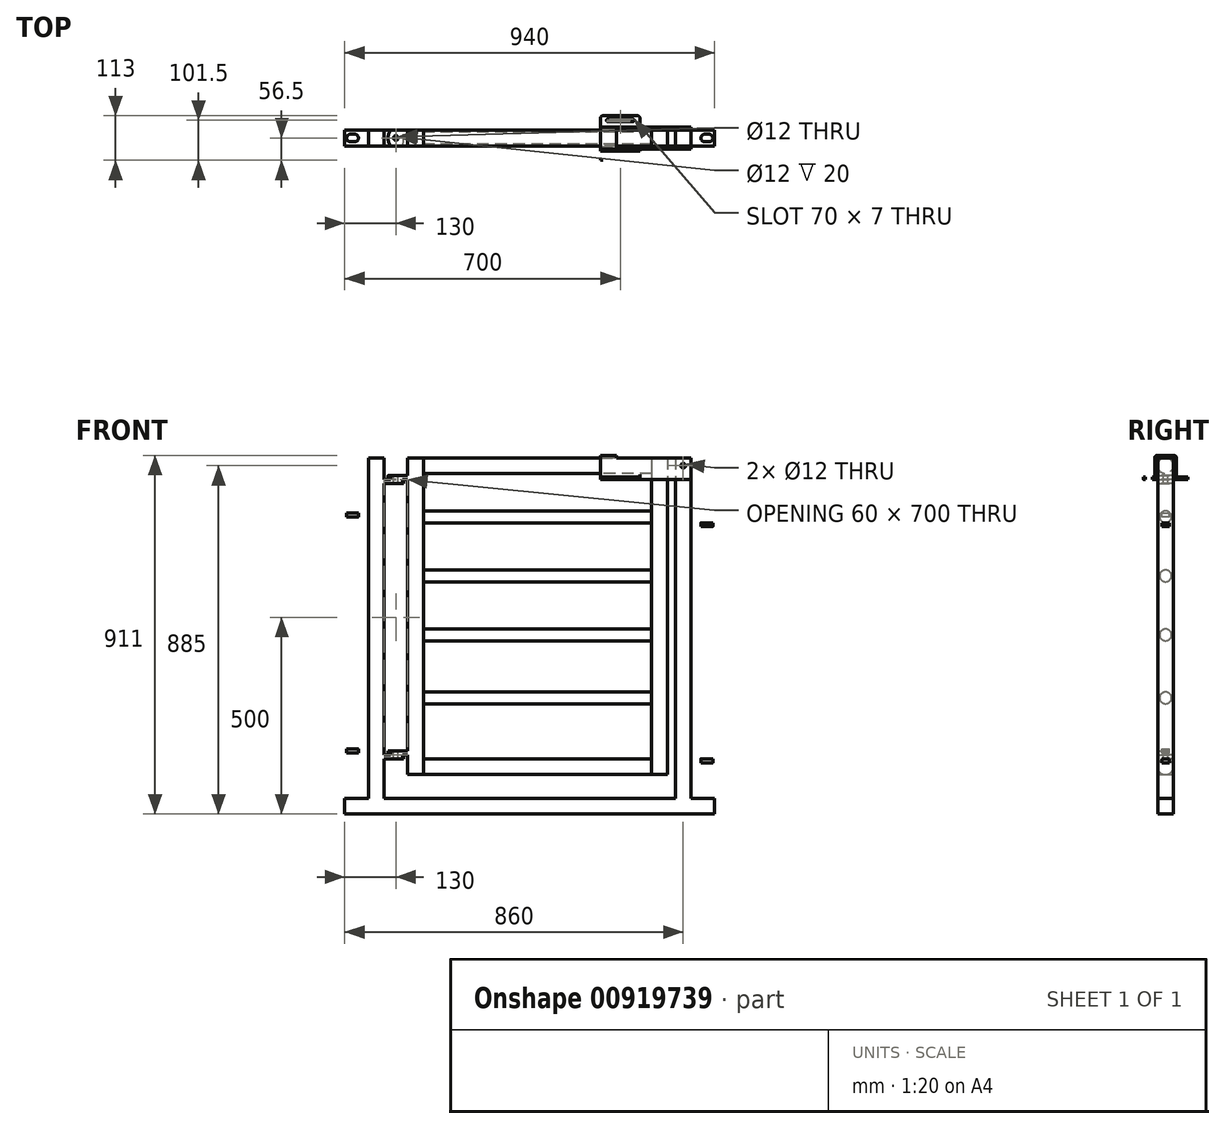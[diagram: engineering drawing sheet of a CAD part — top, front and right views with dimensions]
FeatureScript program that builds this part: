
annotation { "Feature Type Name" : "Feature", "Feature Type Description" : "" }
export const myFeature = defineFeature(function(context is Context, id is Id, definition is map)
    precondition{}
    {
        {
            var Q0;
            Q0=qCreatedBy(makeId("Right.planeOp"),FACE);
            var sketch = newSketch(context, id + "F0", { "sketchPlane" : qUnion([Q0])});
            skLineSegment(sketch, "E0.bottom", {"start": v(-20, 402.5) * mm, "end": v(20, 402.5) * mm});
            skLineSegment(sketch, "E0.top", {"start": v(-20, -402.5) * mm, "end": v(20, -402.5) * mm});
            skLineSegment(sketch, "E0.left", {"start": v(-20, 402.5) * mm, "end": v(-20, -402.5) * mm});
            skLineSegment(sketch, "E0.right", {"start": v(20, 402.5) * mm, "end": v(20, -402.5) * mm});
            skPoint(sketch, "E0.middle", {"position": v(0, 0) * mm});
            skLineSegment(sketch, "E1", {"start": v(0, 402.5) * mm, "end": v(0, -402.5) * mm, "construction": true});
            skPoint(sketch, "E2", {"position": v(0, 382.5) * mm});
            skCircle(sketch, "E3", {"center": v(0, 382.5) * mm, "radius": 20 * mm});
            skPoint(sketch, "E4", {"position": v(0, 252.5) * mm});
            skPoint(sketch, "E5", {"position": v(0, 362.5) * mm});
            skCircle(sketch, "E6", {"center": v(0, 252.5) * mm, "radius": 15 * mm});
            skPoint(sketch, "E7", {"position": v(0, 102.5) * mm});
            skCircle(sketch, "E8", {"center": v(0, 102.5) * mm, "radius": 15 * mm});
            skPoint(sketch, "E9", {"position": v(0, -47.5) * mm});
            skCircle(sketch, "E10", {"center": v(0, -47.5) * mm, "radius": 15 * mm});
            skPoint(sketch, "E11", {"position": v(0, -207.5) * mm});
            skCircle(sketch, "E12", {"center": v(0, -207.5) * mm, "radius": 15 * mm});
            skPoint(sketch, "E13", {"position": v(0, -382.5) * mm});
            skCircle(sketch, "E14", {"center": v(0, -382.5) * mm, "radius": 20 * mm});
            skSolve(sketch);
        }
        {
            var Q0;
            {var subQ0=sQuery(id+"F0.wireOp",EDGE,"E0.left");var subQ1=sQuery(id+"F0.wireOp",EDGE,"E0.bottom");var subQ2=makeQuery(id+"F0.imprint","INTERSECT",VERTEX,{"derivedFrom":[subQ1,subQ0]});Q0=makeQuery(id+"F0.imprint","IMPRINT",FACE,{"disambiguationData":[TD([[makeQuery(id+"F0.imprint","IMPRINT",EDGE,{"disambiguationData":[TD([[subQ2,-1.0]])],"derivedFrom":subQ1}),-1.0]])]});}
            var Q1;
            {var subQ0=sQuery(id+"F0.wireOp",EDGE,"E0.right");var subQ1=sQuery(id+"F0.wireOp",EDGE,"E0.bottom");var subQ2=makeQuery(id+"F0.imprint","INTERSECT",VERTEX,{"derivedFrom":[subQ1,subQ0]});Q1=makeQuery(id+"F0.imprint","IMPRINT",FACE,{"disambiguationData":[TD([[makeQuery(id+"F0.imprint","IMPRINT",EDGE,{"disambiguationData":[TD([[subQ2,1.0]])],"derivedFrom":subQ1}),-1.0]])]});}
            var Q2;
            Q2=makeQuery(id+"F0.imprint","IMPRINT",FACE,{"disambiguationData":[TD([[makeQuery(id+"F0.imprint","IMPRINT",EDGE,{"derivedFrom":sQuery(id+"F0.wireOp",EDGE,"E6")}),-1.0]])]});
            var Q3;
            {var subQ0=sQuery(id+"F0.wireOp",EDGE,"E0.right");var subQ1=sQuery(id+"F0.wireOp",EDGE,"E0.top");var subQ2=makeQuery(id+"F0.imprint","INTERSECT",VERTEX,{"derivedFrom":[subQ1,subQ0]});Q3=makeQuery(id+"F0.imprint","IMPRINT",FACE,{"disambiguationData":[TD([[makeQuery(id+"F0.imprint","IMPRINT",EDGE,{"disambiguationData":[TD([[subQ2,1.0]])],"derivedFrom":subQ1}),1.0]])]});}
            var Q4;
            {var subQ0=sQuery(id+"F0.wireOp",EDGE,"E0.left");var subQ1=sQuery(id+"F0.wireOp",EDGE,"E0.top");var subQ2=makeQuery(id+"F0.imprint","INTERSECT",VERTEX,{"derivedFrom":[subQ1,subQ0]});Q4=makeQuery(id+"F0.imprint","IMPRINT",FACE,{"disambiguationData":[TD([[makeQuery(id+"F0.imprint","IMPRINT",EDGE,{"disambiguationData":[TD([[subQ2,-1.0]])],"derivedFrom":subQ1}),1.0]])]});}
            var Q5;
            {var subQ0=sQuery(id+"F0.wireOp",EDGE,"E3");var subQ1=makeQuery(id+"F0.imprint","INTERSECT",VERTEX,{"derivedFrom":[sQuery(id+"F0.wireOp",EDGE,"E0.bottom"),subQ0]});Q5=makeQuery(id+"F0.imprint","IMPRINT",FACE,{"disambiguationData":[TD([[makeQuery(id+"F0.imprint","IMPRINT",EDGE,{"disambiguationData":[TD([[subQ1,1.0]])],"derivedFrom":subQ0}),1.0]])]});}
            var Q6;
            Q6=makeQuery(id+"F0.imprint","IMPRINT",FACE,{"disambiguationData":[TD([[makeQuery(id+"F0.imprint","IMPRINT",EDGE,{"derivedFrom":sQuery(id+"F0.wireOp",EDGE,"E6")}),1.0]])]});
            var Q7;
            Q7=makeQuery(id+"F0.imprint","IMPRINT",FACE,{"disambiguationData":[TD([[makeQuery(id+"F0.imprint","IMPRINT",EDGE,{"derivedFrom":sQuery(id+"F0.wireOp",EDGE,"E8")}),1.0]])]});
            var Q8;
            Q8=makeQuery(id+"F0.imprint","IMPRINT",FACE,{"disambiguationData":[TD([[makeQuery(id+"F0.imprint","IMPRINT",EDGE,{"derivedFrom":sQuery(id+"F0.wireOp",EDGE,"E10")}),1.0]])]});
            var Q9;
            Q9=makeQuery(id+"F0.imprint","IMPRINT",FACE,{"disambiguationData":[TD([[makeQuery(id+"F0.imprint","IMPRINT",EDGE,{"derivedFrom":sQuery(id+"F0.wireOp",EDGE,"E12")}),1.0]])]});
            var Q10;
            {var subQ0=sQuery(id+"F0.wireOp",EDGE,"E14");var subQ1=makeQuery(id+"F0.imprint","INTERSECT",VERTEX,{"derivedFrom":[sQuery(id+"F0.wireOp",EDGE,"E0.left"),subQ0]});Q10=makeQuery(id+"F0.imprint","IMPRINT",FACE,{"disambiguationData":[TD([[makeQuery(id+"F0.imprint","IMPRINT",EDGE,{"disambiguationData":[TD([[subQ1,1.0]])],"derivedFrom":subQ0}),1.0]])]});}
            extrude(context, id + "F1", {"entities" : qUnion([Q0, Q1, Q2, Q3, Q4, Q5, Q6, Q7, Q8, Q9, Q10]), "depth" : 40 * mm, "offsetDistance" : 25 * mm});
        }
        {
            var Q0;
            Q0=makeQuery(id+"F1.opExtrude","CAP_FACE",FACE,{"disambiguationData":[OSD([sQuery(id+"F0.wireOp",EDGE,"E0.bottom"),sQuery(id+"F0.wireOp",EDGE,"E0.top"),sQuery(id+"F0.wireOp",EDGE,"E0.left"),sQuery(id+"F0.wireOp",EDGE,"E0.right")])],"isStart":false});
            cPlane(context, id + "F2", {"entities" : qUnion([Q0]), "cplaneType" : CPlaneType.OFFSET, "offset" : (580 / 2) * mm, "width" : 150 * mm, "height" : 150 * mm});
        }
        {
            var Q0;
            Q0=makeQuery(id+"F1.opExtrude","SWEPT_BODY",BODY,{"disambiguationData":[OSD([sQuery(id+"F0.wireOp",EDGE,"E0.bottom"),sQuery(id+"F0.wireOp",EDGE,"E0.top"),sQuery(id+"F0.wireOp",EDGE,"E0.left"),sQuery(id+"F0.wireOp",EDGE,"E0.right")])]});
            var Q1;
            Q1=qCreatedBy(id+"F2.planeOp",FACE);
            mirror(context, id + "F3", {"entities" : qUnion([Q0]), "mirrorPlane" : qUnion([Q1])});
        }
        {
            var Q0;
            {var subQ0=sQuery(id+"F0.wireOp",EDGE,"E3");var subQ1=makeQuery(id+"F0.imprint","INTERSECT",VERTEX,{"derivedFrom":[sQuery(id+"F0.wireOp",EDGE,"E0.bottom"),subQ0]});Q0=makeQuery(id+"F0.imprint","IMPRINT",FACE,{"disambiguationData":[TD([[makeQuery(id+"F0.imprint","IMPRINT",EDGE,{"disambiguationData":[TD([[subQ1,1.0]])],"derivedFrom":subQ0}),1.0]])]});}
            var Q1;
            Q1=makeQuery(id+"F0.imprint","IMPRINT",FACE,{"disambiguationData":[TD([[makeQuery(id+"F0.imprint","IMPRINT",EDGE,{"derivedFrom":sQuery(id+"F0.wireOp",EDGE,"E6")}),1.0]])]});
            var Q2;
            Q2=makeQuery(id+"F0.imprint","IMPRINT",FACE,{"disambiguationData":[TD([[makeQuery(id+"F0.imprint","IMPRINT",EDGE,{"derivedFrom":sQuery(id+"F0.wireOp",EDGE,"E8")}),1.0]])]});
            var Q3;
            Q3=makeQuery(id+"F0.imprint","IMPRINT",FACE,{"disambiguationData":[TD([[makeQuery(id+"F0.imprint","IMPRINT",EDGE,{"derivedFrom":sQuery(id+"F0.wireOp",EDGE,"E10")}),1.0]])]});
            var Q4;
            Q4=makeQuery(id+"F0.imprint","IMPRINT",FACE,{"disambiguationData":[TD([[makeQuery(id+"F0.imprint","IMPRINT",EDGE,{"derivedFrom":sQuery(id+"F0.wireOp",EDGE,"E12")}),1.0]])]});
            var Q5;
            {var subQ0=sQuery(id+"F0.wireOp",EDGE,"E14");var subQ1=makeQuery(id+"F0.imprint","INTERSECT",VERTEX,{"derivedFrom":[sQuery(id+"F0.wireOp",EDGE,"E0.left"),subQ0]});Q5=makeQuery(id+"F0.imprint","IMPRINT",FACE,{"disambiguationData":[TD([[makeQuery(id+"F0.imprint","IMPRINT",EDGE,{"disambiguationData":[TD([[subQ1,1.0]])],"derivedFrom":subQ0}),1.0]])]});}
            var Q6;
            Q6=makeQuery(id+"F3.opPattern","COPY",FACE,{"derivedFrom":makeQuery(id+"F1.opExtrude","CAP_FACE",FACE,{"disambiguationData":[OSD([sQuery(id+"F0.wireOp",EDGE,"E0.bottom"),sQuery(id+"F0.wireOp",EDGE,"E0.top"),sQuery(id+"F0.wireOp",EDGE,"E0.left"),sQuery(id+"F0.wireOp",EDGE,"E0.right")])],"isStart":false}),"instanceName":"1"});
            extrude(context, id + "F4", {"entities" : qUnion([Q0, Q1, Q2, Q3, Q4, Q5]), "operationType" : NewBodyOperationType.ADD, "endBound" : BoundingType.UP_TO_SURFACE, "depth" : 25 * mm, "endBoundEntityFace" : qUnion([Q6]), "offsetDistance" : 25 * mm});
        }
        {
            var Q0;
            Q0=makeQuery(id+"F1.opExtrude","CAP_FACE",FACE,{"disambiguationData":[OSD([sQuery(id+"F0.wireOp",EDGE,"E0.bottom"),sQuery(id+"F0.wireOp",EDGE,"E0.top"),sQuery(id+"F0.wireOp",EDGE,"E0.left"),sQuery(id+"F0.wireOp",EDGE,"E0.right")])],"isStart":true});
            var sketch = newSketch(context, id + "F5", { "sketchPlane" : qUnion([Q0])});
            skLineSegment(sketch, "E15.0.0", {"start": v(-20, 402.5) * mm, "end": v(-20, -402.5) * mm});
            skLineSegment(sketch, "E15.0.1", {"start": v(-20, -402.5) * mm, "end": v(20, -402.5) * mm});
            skLineSegment(sketch, "E15.0.2", {"start": v(20, -402.5) * mm, "end": v(20, 402.5) * mm});
            skLineSegment(sketch, "E15.0.3", {"start": v(20, 402.5) * mm, "end": v(-20, 402.5) * mm});
            skLineSegment(sketch, "E16.bottom", {"start": v(20, 357.5) * mm, "end": v(-20, 357.5) * mm});
            skLineSegment(sketch, "E16.top", {"start": v(20, 347.5) * mm, "end": v(-20, 347.5) * mm});
            skLineSegment(sketch, "E16.left", {"start": v(20, 357.5) * mm, "end": v(20, 347.5) * mm});
            skLineSegment(sketch, "E16.right", {"start": v(-20, 357.5) * mm, "end": v(-20, 347.5) * mm});
            skLineSegment(sketch, "E17.bottom", {"start": v(20, -342.5) * mm, "end": v(-20, -342.5) * mm});
            skLineSegment(sketch, "E17.top", {"start": v(20, -352.5) * mm, "end": v(-20, -352.5) * mm});
            skLineSegment(sketch, "E17.left", {"start": v(20, -342.5) * mm, "end": v(20, -352.5) * mm});
            skLineSegment(sketch, "E17.right", {"start": v(-20, -342.5) * mm, "end": v(-20, -352.5) * mm});
            skSolve(sketch);
        }
        {
            var Q0;
            Q0=makeQuery(id+"F5.imprint","IMPRINT",FACE,{"disambiguationData":[TD([[makeQuery(id+"F5.imprint","IMPRINT",EDGE,{"derivedFrom":sQuery(id+"F5.wireOp",EDGE,"E17.bottom")}),1.0]])]});
            var Q1;
            Q1=makeQuery(id+"F5.imprint","IMPRINT",FACE,{"disambiguationData":[TD([[makeQuery(id+"F5.imprint","IMPRINT",EDGE,{"derivedFrom":sQuery(id+"F5.wireOp",EDGE,"E16.bottom")}),1.0]])]});
            extrude(context, id + "F6", {"entities" : qUnion([Q0, Q1]), "operationType" : NewBodyOperationType.ADD, "depth" : 50 * mm, "offsetDistance" : 25 * mm});
        }
        {
            var Q0;
            Q0=makeQuery(id+"F6.opExtrude","SWEPT_FACE",FACE,{"disambiguationData":[OSD([sQuery(id+"F5.wireOp",EDGE,"E16.bottom")])]});
            var sketch = newSketch(context, id + "F7", { "sketchPlane" : qUnion([Q0])});
            skLineSegment(sketch, "E18.0.0", {"start": v(0, -20) * mm, "end": v(0, 20) * mm});
            skLineSegment(sketch, "E18.0.1", {"start": v(0, 20) * mm, "end": v(-50, 20) * mm});
            skLineSegment(sketch, "E18.0.2", {"start": v(-50, 20) * mm, "end": v(-50, -20) * mm});
            skLineSegment(sketch, "E18.0.3", {"start": v(-50, -20) * mm, "end": v(0, -20) * mm});
            skLineSegment(sketch, "E19", {"start": v(-30, 0) * mm, "end": v(0, 0) * mm, "construction": true});
            skPoint(sketch, "E20", {"position": v(-30, 0) * mm});
            skPoint(sketch, "E21", {"position": v(-50, 0) * mm});
            skLineSegment(sketch, "E22", {"start": v(-44.1, 20) * mm, "end": v(-44.1, -20) * mm, "construction": true});
            skArc(sketch, "E23", {"start": v(-44.1, 20) * mm, "mid": v(-50, 0) * mm, "end": v(-44.1, -20) * mm});
            skSolve(sketch);
        }
        {
            var Q0;
            Q0=sQuery(id+"F7.wireOp",VERTEX,"E20");
            var Q1;
            Q1=makeQuery(id+"F1.opExtrude","SWEPT_BODY",BODY,{"disambiguationData":[OSD([sQuery(id+"F0.wireOp",EDGE,"E0.bottom"),sQuery(id+"F0.wireOp",EDGE,"E0.top"),sQuery(id+"F0.wireOp",EDGE,"E0.left"),sQuery(id+"F0.wireOp",EDGE,"E0.right")])]});
            hole(context, id + "F8", {"style" : HoleStyle.SIMPLE, "endStyle" : HoleEndStyle.THROUGH, "standardTappedOrClearance" : lookupTablePath({ "standard" : "ISO", "size" : "12", "type" : "Drilled" }), "standardBlindInLast" : lookupTablePath({ "standard" : "ISO", "size" : "12", "type" : "Drilled" }), "holeDiameter" : 12 * mm, "majorDiameter" : 5 * mm, "isTappedThrough" : true, "tappedDepth" : 12 * mm, "tapClearance" : 3, "startFromSketch" : true, "locations" : qUnion([Q0]), "scope" : qUnion([Q1])});
        }
        {
            var Q0;
            {var subQ0=sQuery(id+"F7.wireOp",EDGE,"E18.0.2");var subQ1=sQuery(id+"F7.wireOp",EDGE,"E18.0.1");var subQ2=makeQuery(id+"F7.imprint","INTERSECT",VERTEX,{"derivedFrom":[subQ1,subQ0]});Q0=makeQuery(id+"F7.imprint","IMPRINT",FACE,{"disambiguationData":[TD([[makeQuery(id+"F7.imprint","IMPRINT",EDGE,{"disambiguationData":[TD([[subQ2,-1.0]])],"derivedFrom":subQ1}),-1.0]])]});}
            var Q1;
            {var subQ0=sQuery(id+"F7.wireOp",EDGE,"E18.0.3");var subQ1=sQuery(id+"F7.wireOp",EDGE,"E18.0.2");var subQ2=makeQuery(id+"F7.imprint","INTERSECT",VERTEX,{"derivedFrom":[subQ1,subQ0]});Q1=makeQuery(id+"F7.imprint","IMPRINT",FACE,{"disambiguationData":[TD([[makeQuery(id+"F7.imprint","IMPRINT",EDGE,{"disambiguationData":[TD([[subQ2,-1.0]])],"derivedFrom":subQ1}),-1.0]])]});}
            extrude(context, id + "F9", {"entities" : qUnion([Q0, Q1]), "operationType" : NewBodyOperationType.REMOVE, "endBound" : BoundingType.THROUGH_ALL, "oppositeDirection" : true, "depth" : 25 * mm, "offsetDistance" : 25 * mm});
        }
        {
            var Q0;
            Q0=qCreatedBy(makeId("Right.planeOp"),FACE);
            cPlane(context, id + "F10", {"entities" : qUnion([Q0]), "cplaneType" : CPlaneType.OFFSET, "offset" : 60 * mm, "oppositeDirection" : true, "width" : 150 * mm, "height" : 150 * mm});
        }
        {
            var Q0;
            Q0=qCreatedBy(id+"F10.planeOp",FACE);
            var sketch = newSketch(context, id + "F11", { "sketchPlane" : qUnion([Q0])});
            skPoint(sketch, "E24.0", {"position": v(20, 402.5) * mm});
            skLineSegment(sketch, "E25.bottom", {"start": v(20, 402.5) * mm, "end": v(-20, 402.5) * mm});
            skLineSegment(sketch, "E25.top", {"start": v(20, -502.5) * mm, "end": v(-20, -502.5) * mm});
            skLineSegment(sketch, "E25.left", {"start": v(20, 402.5) * mm, "end": v(20, -502.5) * mm});
            skLineSegment(sketch, "E25.right", {"start": v(-20, 402.5) * mm, "end": v(-20, -502.5) * mm});
            skSolve(sketch);
        }
        {
            var Q0;
            Q0=makeQuery(id+"F11.imprint","IMPRINT",FACE,{"disambiguationData":[TD([[makeQuery(id+"F11.imprint","IMPRINT",EDGE,{"derivedFrom":sQuery(id+"F11.wireOp",EDGE,"E25.bottom")}),1.0]])]});
            extrude(context, id + "F12", {"entities" : qUnion([Q0]), "oppositeDirection" : true, "depth" : 40 * mm, "offsetDistance" : 25 * mm});
        }
        {
            var Q0;
            Q0=makeQuery(id+"F12.opExtrude","CAP_FACE",FACE,{"disambiguationData":[OSD([sQuery(id+"F11.wireOp",EDGE,"E25.bottom"),sQuery(id+"F11.wireOp",EDGE,"E25.top"),sQuery(id+"F11.wireOp",EDGE,"E25.left"),sQuery(id+"F11.wireOp",EDGE,"E25.right")])],"isStart":false});
            var sketch = newSketch(context, id + "F13", { "sketchPlane" : qUnion([Q0])});
            skLineSegment(sketch, "E26.0.0", {"start": v(-20, -502.5) * mm, "end": v(20, -502.5) * mm});
            skLineSegment(sketch, "E26.0.1", {"start": v(20, -502.5) * mm, "end": v(20, 402.5) * mm});
            skLineSegment(sketch, "E26.0.2", {"start": v(20, 402.5) * mm, "end": v(-20, 402.5) * mm});
            skLineSegment(sketch, "E26.0.3", {"start": v(-20, 402.5) * mm, "end": v(-20, -502.5) * mm});
            skLineSegment(sketch, "E27.top", {"start": v(-20, -462.5) * mm, "end": v(20, -462.5) * mm});
            skLineSegment(sketch, "E27.left", {"start": v(-20, -502.5) * mm, "end": v(-20, -462.5) * mm});
            skLineSegment(sketch, "E27.right", {"start": v(20, -502.5) * mm, "end": v(20, -462.5) * mm});
            skSolve(sketch);
        }
        {
            var Q0;
            Q0=makeQuery(id+"F13.imprint","IMPRINT",FACE,{"disambiguationData":[TD([[makeQuery(id+"F13.imprint","IMPRINT",EDGE,{"derivedFrom":sQuery(id+"F13.wireOp",EDGE,"E26.0.0")}),1.0]])]});
            extrude(context, id + "F14", {"entities" : qUnion([Q0]), "oppositeDirection" : true, "depth" : 880 * mm, "offsetDistance" : 25 * mm, "hasSecondDirection" : true, "secondDirectionOppositeDirection" : false, "secondDirectionDepth" : 60 * mm});
        }
        {
            var Q0;
            Q0=makeQuery(id+"F12.opExtrude","CAP_FACE",FACE,{"disambiguationData":[OSD([sQuery(id+"F11.wireOp",EDGE,"E25.bottom"),sQuery(id+"F11.wireOp",EDGE,"E25.top"),sQuery(id+"F11.wireOp",EDGE,"E25.left"),sQuery(id+"F11.wireOp",EDGE,"E25.right")])],"isStart":true});
            cPlane(context, id + "F15", {"entities" : qUnion([Q0]), "cplaneType" : CPlaneType.OFFSET, "offset" : (740 / 2) * mm, "width" : 150 * mm, "height" : 150 * mm});
        }
        {
            var Q0;
            Q0=makeQuery(id+"F12.opExtrude","SWEPT_BODY",BODY,{"disambiguationData":[OSD([sQuery(id+"F11.wireOp",EDGE,"E25.bottom"),sQuery(id+"F11.wireOp",EDGE,"E25.top"),sQuery(id+"F11.wireOp",EDGE,"E25.left"),sQuery(id+"F11.wireOp",EDGE,"E25.right")])]});
            var Q1;
            Q1=qCreatedBy(id+"F15.planeOp",FACE);
            mirror(context, id + "F16", {"operationType" : NewBodyOperationType.ADD, "entities" : qUnion([Q0]), "mirrorPlane" : qUnion([Q1])});
        }
        {
            var Q0;
            Q0=makeQuery(id+"F16.opPattern","COPY",FACE,{"derivedFrom":makeQuery(id+"F12.opExtrude","CAP_FACE",FACE,{"disambiguationData":[OSD([sQuery(id+"F11.wireOp",EDGE,"E25.bottom"),sQuery(id+"F11.wireOp",EDGE,"E25.top"),sQuery(id+"F11.wireOp",EDGE,"E25.left"),sQuery(id+"F11.wireOp",EDGE,"E25.right")])],"isStart":false}),"instanceName":"1"});
            var sketch = newSketch(context, id + "F17", { "sketchPlane" : qUnion([Q0])});
            skLineSegment(sketch, "E28.0.0", {"start": v(-20, 402.5) * mm, "end": v(-20, -462.5) * mm});
            skLineSegment(sketch, "E28.0.1", {"start": v(-20, -462.5) * mm, "end": v(20, -462.5) * mm});
            skLineSegment(sketch, "E28.0.2", {"start": v(20, -462.5) * mm, "end": v(20, 402.5) * mm});
            skLineSegment(sketch, "E28.0.3", {"start": v(20, 402.5) * mm, "end": v(-20, 402.5) * mm});
            skLineSegment(sketch, "E29.bottom", {"start": v(-20, 237.5) * mm, "end": v(20, 237.5) * mm});
            skLineSegment(sketch, "E29.top", {"start": v(-20, 227.5) * mm, "end": v(20, 227.5) * mm});
            skLineSegment(sketch, "E29.left", {"start": v(-20, 237.5) * mm, "end": v(-20, 227.5) * mm});
            skLineSegment(sketch, "E29.right", {"start": v(20, 237.5) * mm, "end": v(20, 227.5) * mm});
            skPoint(sketch, "E30.0", {"position": v(0, -502.5) * mm});
            skLineSegment(sketch, "E31.bottom", {"start": v(-20, -362.5) * mm, "end": v(20, -362.5) * mm});
            skLineSegment(sketch, "E31.top", {"start": v(-20, -372.5) * mm, "end": v(20, -372.5) * mm});
            skLineSegment(sketch, "E31.left", {"start": v(-20, -362.5) * mm, "end": v(-20, -372.5) * mm});
            skLineSegment(sketch, "E31.right", {"start": v(20, -362.5) * mm, "end": v(20, -372.5) * mm});
            skSolve(sketch);
        }
        {
            var Q0;
            Q0=makeQuery(id+"F17.imprint","IMPRINT",FACE,{"disambiguationData":[TD([[makeQuery(id+"F17.imprint","IMPRINT",EDGE,{"derivedFrom":sQuery(id+"F17.wireOp",EDGE,"E29.bottom")}),-1.0]])]});
            var Q1;
            Q1=makeQuery(id+"F17.imprint","IMPRINT",FACE,{"disambiguationData":[TD([[makeQuery(id+"F17.imprint","IMPRINT",EDGE,{"derivedFrom":sQuery(id+"F17.wireOp",EDGE,"E31.bottom")}),-1.0]])]});
            extrude(context, id + "F18", {"entities" : qUnion([Q0, Q1]), "operationType" : NewBodyOperationType.ADD, "depth" : 65 * mm, "offsetDistance" : 25 * mm});
        }
        {
            var Q0;
            Q0=makeQuery(id+"F12.opExtrude","CAP_FACE",FACE,{"disambiguationData":[OSD([sQuery(id+"F11.wireOp",EDGE,"E25.bottom"),sQuery(id+"F11.wireOp",EDGE,"E25.top"),sQuery(id+"F11.wireOp",EDGE,"E25.left"),sQuery(id+"F11.wireOp",EDGE,"E25.right")])],"isStart":false});
            var sketch = newSketch(context, id + "F19", { "sketchPlane" : qUnion([Q0])});
            skLineSegment(sketch, "E32.0.0", {"start": v(-20, -462.5) * mm, "end": v(20, -462.5) * mm});
            skLineSegment(sketch, "E32.0.1", {"start": v(20, -462.5) * mm, "end": v(20, 402.5) * mm});
            skLineSegment(sketch, "E32.0.2", {"start": v(20, 402.5) * mm, "end": v(-20, 402.5) * mm});
            skLineSegment(sketch, "E32.0.3", {"start": v(-20, 402.5) * mm, "end": v(-20, -462.5) * mm});
            skLineSegment(sketch, "E33.0.0", {"start": v(20, -462.5) * mm, "end": v(-20, -462.5) * mm});
            skLineSegment(sketch, "E33.0.1", {"start": v(-20, -462.5) * mm, "end": v(-20, -502.5) * mm});
            skLineSegment(sketch, "E33.0.2", {"start": v(-20, -502.5) * mm, "end": v(20, -502.5) * mm});
            skLineSegment(sketch, "E33.0.3", {"start": v(20, -502.5) * mm, "end": v(20, -462.5) * mm});
            skLineSegment(sketch, "E34.bottom", {"start": v(20, -347.5) * mm, "end": v(-20, -347.5) * mm});
            skLineSegment(sketch, "E34.top", {"start": v(20, -337.5) * mm, "end": v(-20, -337.5) * mm});
            skLineSegment(sketch, "E34.left", {"start": v(20, -347.5) * mm, "end": v(20, -337.5) * mm});
            skLineSegment(sketch, "E34.right", {"start": v(-20, -347.5) * mm, "end": v(-20, -337.5) * mm});
            skLineSegment(sketch, "E35.bottom", {"start": v(-20, 252.5) * mm, "end": v(20, 252.5) * mm});
            skLineSegment(sketch, "E35.top", {"start": v(-20, 262.5) * mm, "end": v(20, 262.5) * mm});
            skLineSegment(sketch, "E35.left", {"start": v(-20, 252.5) * mm, "end": v(-20, 262.5) * mm});
            skLineSegment(sketch, "E35.right", {"start": v(20, 252.5) * mm, "end": v(20, 262.5) * mm});
            skSolve(sketch);
        }
        {
            var Q0;
            Q0=makeQuery(id+"F19.imprint","IMPRINT",FACE,{"disambiguationData":[TD([[makeQuery(id+"F19.imprint","IMPRINT",EDGE,{"derivedFrom":sQuery(id+"F19.wireOp",EDGE,"E35.bottom")}),1.0]])]});
            var Q1;
            Q1=makeQuery(id+"F19.imprint","IMPRINT",FACE,{"disambiguationData":[TD([[makeQuery(id+"F19.imprint","IMPRINT",EDGE,{"derivedFrom":sQuery(id+"F19.wireOp",EDGE,"E34.bottom")}),-1.0]])]});
            extrude(context, id + "F20", {"entities" : qUnion([Q0, Q1]), "operationType" : NewBodyOperationType.ADD, "depth" : 65 * mm, "offsetDistance" : 25 * mm});
        }
        {
            var Q0;
            Q0=makeQuery(id+"F20.opExtrude","SWEPT_FACE",FACE,{"disambiguationData":[OSD([sQuery(id+"F19.wireOp",EDGE,"E35.top")])]});
            var sketch = newSketch(context, id + "F21", { "sketchPlane" : qUnion([Q0])});
            skLineSegment(sketch, "E36.0.0", {"start": v(-100, -20) * mm, "end": v(-100, 20) * mm});
            skLineSegment(sketch, "E36.0.1", {"start": v(-100, 20) * mm, "end": v(-165, 20) * mm});
            skLineSegment(sketch, "E36.0.2", {"start": v(-165, 20) * mm, "end": v(-165, -20) * mm});
            skLineSegment(sketch, "E36.0.3", {"start": v(-165, -20) * mm, "end": v(-100, -20) * mm});
            skLineSegment(sketch, "E37.0.0", {"start": v(720, 20) * mm, "end": v(720, -20) * mm});
            skLineSegment(sketch, "E37.0.1", {"start": v(720, -20) * mm, "end": v(785, -20) * mm});
            skLineSegment(sketch, "E37.0.2", {"start": v(785, -20) * mm, "end": v(785, 20) * mm});
            skLineSegment(sketch, "E37.0.3", {"start": v(785, 20) * mm, "end": v(720, 20) * mm});
            skLineSegment(sketch, "E38", {"start": v(-100, 0) * mm, "end": v(-134.5, 0) * mm, "construction": true});
            skLineSegment(sketch, "E39", {"start": v(-134.5, 0) * mm, "end": v(-145.5, 0) * mm});
            skArc(sketch, "E40.0.startCap", {"start": v(-134.5, 9.5) * mm, "mid": v(-125, 0) * mm, "end": v(-134.5, -9.5) * mm});
            skArc(sketch, "E40.0.endCap", {"start": v(-145.5, -9.5) * mm, "mid": v(-155, 0) * mm, "end": v(-145.5, 9.5) * mm});
            skLineSegment(sketch, "E40.0.left", {"start": v(-134.5, -9.5) * mm, "end": v(-145.5, -9.5) * mm});
            skLineSegment(sketch, "E40.0.right", {"start": v(-134.5, 9.5) * mm, "end": v(-145.5, 9.5) * mm});
            skLineSegment(sketch, "E41", {"start": v(720, 0) * mm, "end": v(754.5, 0) * mm, "construction": true});
            skLineSegment(sketch, "E42", {"start": v(754.5, 0) * mm, "end": v(765.5, 0) * mm});
            skArc(sketch, "E43.0.startCap", {"start": v(754.5, -9.5) * mm, "mid": v(745, 0) * mm, "end": v(754.5, 9.5) * mm});
            skArc(sketch, "E43.0.endCap", {"start": v(765.5, 9.5) * mm, "mid": v(775, 0) * mm, "end": v(765.5, -9.5) * mm});
            skLineSegment(sketch, "E43.0.left", {"start": v(754.5, 9.5) * mm, "end": v(765.5, 9.5) * mm});
            skLineSegment(sketch, "E43.0.right", {"start": v(754.5, -9.5) * mm, "end": v(765.5, -9.5) * mm});
            skLineSegment(sketch, "E44", {"start": v(-159, 20) * mm, "end": v(-159, -20) * mm, "construction": true});
            skPoint(sketch, "E45", {"position": v(-165, 0) * mm});
            skLineSegment(sketch, "E46", {"start": v(779, 20) * mm, "end": v(779, -20) * mm, "construction": true});
            skPoint(sketch, "E47", {"position": v(785, 0) * mm});
            skArc(sketch, "E48", {"start": v(779, -20) * mm, "mid": v(785, 0) * mm, "end": v(779, 20) * mm});
            skArc(sketch, "E49", {"start": v(-159, 20) * mm, "mid": v(-165, 0) * mm, "end": v(-159, -20) * mm});
            skSolve(sketch);
        }
        {
            var Q0;
            {var subQ0=sQuery(id+"F21.wireOp",EDGE,"E36.0.2");var subQ1=sQuery(id+"F21.wireOp",EDGE,"E36.0.1");var subQ2=makeQuery(id+"F21.imprint","INTERSECT",VERTEX,{"derivedFrom":[subQ1,subQ0]});Q0=makeQuery(id+"F21.imprint","IMPRINT",FACE,{"disambiguationData":[TD([[makeQuery(id+"F21.imprint","IMPRINT",EDGE,{"disambiguationData":[TD([[subQ2,-1.0]])],"derivedFrom":subQ1}),-1.0]])]});}
            var Q1;
            {var subQ0=sQuery(id+"F21.wireOp",EDGE,"E36.0.3");var subQ1=sQuery(id+"F21.wireOp",EDGE,"E36.0.2");var subQ2=makeQuery(id+"F21.imprint","INTERSECT",VERTEX,{"derivedFrom":[subQ1,subQ0]});Q1=makeQuery(id+"F21.imprint","IMPRINT",FACE,{"disambiguationData":[TD([[makeQuery(id+"F21.imprint","IMPRINT",EDGE,{"disambiguationData":[TD([[subQ2,1.0]])],"derivedFrom":subQ1}),1.0]])]});}
            var Q2;
            Q2=makeQuery(id+"F21.imprint","IMPRINT",FACE,{"disambiguationData":[TD([[makeQuery(id+"F21.imprint","IMPRINT",EDGE,{"derivedFrom":sQuery(id+"F21.wireOp",EDGE,"E40.0.startCap")}),-1.0]])]});
            var Q3;
            Q3=makeQuery(id+"F21.imprint","IMPRINT",FACE,{"disambiguationData":[TD([[makeQuery(id+"F21.imprint","IMPRINT",EDGE,{"derivedFrom":sQuery(id+"F21.wireOp",EDGE,"E43.0.startCap")}),-1.0]])]});
            var Q4;
            {var subQ0=sQuery(id+"F21.wireOp",EDGE,"E37.0.3");var subQ1=sQuery(id+"F21.wireOp",EDGE,"E37.0.2");var subQ2=makeQuery(id+"F21.imprint","INTERSECT",VERTEX,{"derivedFrom":[subQ1,subQ0]});Q4=makeQuery(id+"F21.imprint","IMPRINT",FACE,{"disambiguationData":[TD([[makeQuery(id+"F21.imprint","IMPRINT",EDGE,{"disambiguationData":[TD([[subQ2,1.0]])],"derivedFrom":subQ1}),1.0]])]});}
            var Q5;
            {var subQ0=sQuery(id+"F21.wireOp",EDGE,"E37.0.2");var subQ1=sQuery(id+"F21.wireOp",EDGE,"E37.0.1");var subQ2=makeQuery(id+"F21.imprint","INTERSECT",VERTEX,{"derivedFrom":[subQ1,subQ0]});Q5=makeQuery(id+"F21.imprint","IMPRINT",FACE,{"disambiguationData":[TD([[makeQuery(id+"F21.imprint","IMPRINT",EDGE,{"disambiguationData":[TD([[subQ2,1.0]])],"derivedFrom":subQ1}),1.0]])]});}
            var Q6;
            Q6=makeQuery(id+"F18.opExtrude","SWEPT_FACE",FACE,{"disambiguationData":[OSD([sQuery(id+"F17.wireOp",EDGE,"E31.top")])]});
            extrude(context, id + "F22", {"entities" : qUnion([Q0, Q1, Q2, Q3, Q4, Q5]), "operationType" : NewBodyOperationType.REMOVE, "endBound" : BoundingType.UP_TO_SURFACE, "oppositeDirection" : true, "depth" : 25 * mm, "endBoundEntityFace" : qUnion([Q6]), "offsetDistance" : 25 * mm});
        }
        {
            var Q0;
            Q0=makeQuery(id+"F6.opExtrude","SWEPT_FACE",FACE,{"disambiguationData":[OSD([sQuery(id+"F5.wireOp",EDGE,"E17.top")])]});
            var sketch = newSketch(context, id + "F23", { "sketchPlane" : qUnion([Q0])});
            skCircle(sketch, "E50.0", {"center": v(-30, 0) * mm, "radius": 6 * mm});
            skLineSegment(sketch, "E51.0", {"start": v(-60, -20) * mm, "end": v(-60, 20) * mm});
            skLineSegment(sketch, "E52", {"start": v(-60, -20) * mm, "end": v(-10, -20) * mm});
            skLineSegment(sketch, "E53", {"start": v(-10, -20) * mm, "end": v(-10, 20) * mm});
            skLineSegment(sketch, "E54", {"start": v(-10, 20) * mm, "end": v(-60, 20) * mm});
            skLineSegment(sketch, "E55", {"start": v(-13, -20) * mm, "end": v(-13, 20) * mm, "construction": true});
            skPoint(sketch, "E56", {"position": v(-10, 0) * mm});
            skArc(sketch, "E57", {"start": v(-13, -20) * mm, "mid": v(-10, 0) * mm, "end": v(-13, 20) * mm});
            skSolve(sketch);
        }
        {
            var Q0;
            Q0=makeQuery(id+"F23.imprint","IMPRINT",FACE,{"disambiguationData":[TD([[makeQuery(id+"F23.imprint","IMPRINT",EDGE,{"derivedFrom":sQuery(id+"F23.wireOp",EDGE,"E50.0")}),1.0]])]});
            var Q1;
            {var subQ0=sQuery(id+"F23.wireOp",EDGE,"E51.0");Q1=makeQuery(id+"F23.imprint","IMPRINT",FACE,{"disambiguationData":[TD([[makeQuery(id+"F23.imprint","IMPRINT",EDGE,{"derivedFrom":subQ0}),-1.0]])]});}
            extrude(context, id + "F24", {"entities" : qUnion([Q0, Q1]), "operationType" : NewBodyOperationType.ADD, "depth" : 10 * mm, "offsetDistance" : 25 * mm});
        }
        {
            var Q0;
            Q0=makeQuery(id+"F6.opExtrude","SWEPT_FACE",FACE,{"disambiguationData":[OSD([sQuery(id+"F5.wireOp",EDGE,"E16.top")])]});
            var sketch = newSketch(context, id + "F25", { "sketchPlane" : qUnion([Q0])});
            skCircle(sketch, "E58.0", {"center": v(-30.01, 0) * mm, "radius": 6 * mm});
            skLineSegment(sketch, "E59.0", {"start": v(-60.01, -20) * mm, "end": v(-60.01, 20) * mm});
            skLineSegment(sketch, "E60", {"start": v(-60.01, -20) * mm, "end": v(-10.01, -20) * mm});
            skLineSegment(sketch, "E61", {"start": v(-10.01, -20) * mm, "end": v(-10.01, 20) * mm});
            skLineSegment(sketch, "E62", {"start": v(-10.01, 20) * mm, "end": v(-60.01, 20) * mm});
            skLineSegment(sketch, "E63", {"start": v(-13.01, -20) * mm, "end": v(-13.01, 20) * mm, "construction": true});
            skPoint(sketch, "E64", {"position": v(-10.01, 0) * mm});
            skArc(sketch, "E65", {"start": v(-13.01, -20) * mm, "mid": v(-10.01, 0) * mm, "end": v(-13.01, 20) * mm});
            skSolve(sketch);
        }
        {
            var Q0;
            {var subQ0=sQuery(id+"F25.wireOp",EDGE,"E65");var subQ1=makeQuery(id+"F25.imprint","INTERSECT",VERTEX,{"derivedFrom":[sQuery(id+"F25.wireOp",EDGE,"E61"),subQ0]});Q0=makeQuery(id+"F25.imprint","IMPRINT",FACE,{"disambiguationData":[TD([[makeQuery(id+"F25.imprint","IMPRINT",EDGE,{"disambiguationData":[TD([[subQ1,-1.0]])],"derivedFrom":subQ0}),1.0]])]});}
            var Q1;
            {var subQ0=sQuery(id+"F25.wireOp",EDGE,"E59.0");Q1=makeQuery(id+"F25.imprint","IMPRINT",FACE,{"disambiguationData":[TD([[makeQuery(id+"F25.imprint","IMPRINT",EDGE,{"derivedFrom":subQ0}),-1.0]])]});}
            extrude(context, id + "F26", {"entities" : qUnion([Q0, Q1]), "operationType" : NewBodyOperationType.ADD, "depth" : 10 * mm, "offsetDistance" : 25 * mm});
        }
        {
            var Q0;
            Q0=makeQuery(id+"F16.opPattern","COPY",FACE,{"derivedFrom":makeQuery(id+"F12.opExtrude","CAP_FACE",FACE,{"disambiguationData":[OSD([sQuery(id+"F11.wireOp",EDGE,"E25.bottom"),sQuery(id+"F11.wireOp",EDGE,"E25.top"),sQuery(id+"F11.wireOp",EDGE,"E25.left"),sQuery(id+"F11.wireOp",EDGE,"E25.right")])],"isStart":true}),"instanceName":"1"});
            var sketch = newSketch(context, id + "F27", { "sketchPlane" : qUnion([Q0])});
            skLineSegment(sketch, "E66", {"start": v(0, 402.5) * mm, "end": v(-21.5, 402.5) * mm});
            skLineSegment(sketch, "E67", {"start": v(0, 402.5) * mm, "end": v(20.5, 402.5) * mm});
            skLineSegment(sketch, "E68", {"start": v(21.5, 401.5) * mm, "end": v(21.5, 350.5) * mm});
            skLineSegment(sketch, "E69", {"start": v(0, 402.5) * mm, "end": v(0, 389.8) * mm, "construction": true});
            skLineSegment(sketch, "E70", {"start": v(24.5, 347.5) * mm, "end": v(56.5, 347.5) * mm});
            skPoint(sketch, "E71.visualSharp", {"position": v(21.5, 402.5) * mm});
            skArc(sketch, "E71.filletArc", {"start": v(21.5, 401.5) * mm, "mid": v(21.2, 402.2) * mm, "end": v(20.5, 402.5) * mm});
            skPoint(sketch, "E72.visualSharp", {"position": v(21.5, 347.5) * mm});
            skArc(sketch, "E72.filletArc", {"start": v(21.5, 350.5) * mm, "mid": v(22.38, 348.38) * mm, "end": v(24.5, 347.5) * mm});
            skLineSegment(sketch, "E73", {"start": v(56.5, 347.5) * mm, "end": v(56.5, 353.5) * mm});
            skLineSegment(sketch, "E74", {"start": v(56.5, 353.5) * mm, "end": v(33.5, 353.5) * mm});
            skLineSegment(sketch, "E75", {"start": v(27.5, 402.5) * mm, "end": v(27.5, 359.5) * mm});
            skPoint(sketch, "E76.newPointB", {"position": v(24.5, 353.5) * mm});
            skArc(sketch, "E76.filletArc", {"start": v(27.5, 359.5) * mm, "mid": v(29.26, 355.26) * mm, "end": v(33.5, 353.5) * mm});
            skLineSegment(sketch, "E77", {"start": v(21.5, 408.5) * mm, "end": v(-32.65, 408.5) * mm});
            skPoint(sketch, "E78.visualSharp", {"position": v(27.5, 408.5) * mm});
            skArc(sketch, "E78.filletArc", {"start": v(27.5, 402.5) * mm, "mid": v(25.74, 406.74) * mm, "end": v(21.5, 408.5) * mm});
            skArc(sketch, "E79.MirrorCS", {"start": v(-27.5, 402.5) * mm, "mid": v(-25.74, 406.74) * mm, "end": v(-21.5, 408.5) * mm});
            skLineSegment(sketch, "E80.MirrorCS", {"start": v(-27.5, 402.5) * mm, "end": v(-27.5, 359.5) * mm});
            skLineSegment(sketch, "E81.MirrorCS", {"start": v(-21.5, 401.5) * mm, "end": v(-21.5, 350.5) * mm});
            skArc(sketch, "E82.MirrorCS", {"start": v(-21.5, 401.5) * mm, "mid": v(-21.2, 402.2) * mm, "end": v(-20.5, 402.5) * mm});
            skArc(sketch, "E83.MirrorCS", {"start": v(-21.5, 350.5) * mm, "mid": v(-22.38, 348.38) * mm, "end": v(-24.5, 347.5) * mm});
            skLineSegment(sketch, "E84.MirrorCS", {"start": v(-24.5, 347.5) * mm, "end": v(-56.5, 347.5) * mm});
            skLineSegment(sketch, "E85.MirrorCS", {"start": v(-56.5, 347.5) * mm, "end": v(-56.5, 353.5) * mm});
            skLineSegment(sketch, "E86.MirrorCS", {"start": v(-56.5, 353.5) * mm, "end": v(-33.5, 353.5) * mm});
            skArc(sketch, "E87.MirrorCS", {"start": v(-27.5, 359.5) * mm, "mid": v(-29.26, 355.26) * mm, "end": v(-33.5, 353.5) * mm});
            skSolve(sketch);
        }
        {
            var Q0;
            Q0=makeQuery(id+"F27.imprint","IMPRINT",FACE,{"disambiguationData":[TD([[makeQuery(id+"F27.imprint","IMPRINT",EDGE,{"derivedFrom":sQuery(id+"F27.wireOp",EDGE,"E68")}),1.0]])]});
            extrude(context, id + "F28", {"entities" : qUnion([Q0]), "depth" : 190 * mm, "offsetDistance" : 25 * mm, "hasSecondDirection" : true, "secondDirectionOppositeDirection" : true, "secondDirectionDepth" : 40 * mm});
        }
        {
            var Q0;
            Q0=makeQuery(id+"F28.opExtrude","SWEPT_FACE",FACE,{"disambiguationData":[OSD([sQuery(id+"F27.wireOp",EDGE,"E75")])]});
            var sketch = newSketch(context, id + "F29", { "sketchPlane" : qUnion([Q0])});
            skLineSegment(sketch, "E88.0", {"start": v(490, 402.5) * mm, "end": v(720, 402.5) * mm});
            skLineSegment(sketch, "E89.0", {"start": v(490, 408.5) * mm, "end": v(720, 408.5) * mm});
            skLineSegment(sketch, "E90.0", {"start": v(720, 402.5) * mm, "end": v(720, 359.5) * mm});
            skLineSegment(sketch, "E91.0", {"start": v(720, 402.5) * mm, "end": v(720, 408.5) * mm});
            skLineSegment(sketch, "E92", {"start": v(530, 408.5) * mm, "end": v(530, 402.5) * mm});
            skLineSegment(sketch, "E93", {"start": v(720, 382.5) * mm, "end": v(700, 382.5) * mm, "construction": true});
            skPoint(sketch, "E94", {"position": v(700, 382.5) * mm});
            skSolve(sketch);
        }
        {
            var Q0;
            {var subQ0=sQuery(id+"F29.wireOp",EDGE,"E91.0");Q0=makeQuery(id+"F29.imprint","IMPRINT",FACE,{"disambiguationData":[TD([[makeQuery(id+"F29.imprint","IMPRINT",EDGE,{"derivedFrom":subQ0}),1.0]])]});}
            extrude(context, id + "F30", {"entities" : qUnion([Q0]), "operationType" : NewBodyOperationType.REMOVE, "endBound" : BoundingType.THROUGH_ALL, "oppositeDirection" : true, "depth" : 25 * mm, "offsetDistance" : 25 * mm});
        }
        {
            var Q0;
            Q0=sQuery(id+"F29.wireOp",VERTEX,"E94");
            var Q1;
            Q1=makeQuery(id+"F12.opExtrude","SWEPT_BODY",BODY,{"disambiguationData":[OSD([sQuery(id+"F11.wireOp",EDGE,"E25.bottom"),sQuery(id+"F11.wireOp",EDGE,"E25.top"),sQuery(id+"F11.wireOp",EDGE,"E25.left"),sQuery(id+"F11.wireOp",EDGE,"E25.right")])]});
            var Q2;
            Q2=makeQuery(id+"F28.opExtrude","SWEPT_BODY",BODY,{"disambiguationData":[OSD([sQuery(id+"F27.wireOp",EDGE,"E66"),sQuery(id+"F27.wireOp",EDGE,"E67"),sQuery(id+"F27.wireOp",EDGE,"E68"),sQuery(id+"F27.wireOp",EDGE,"E70"),sQuery(id+"F27.wireOp",EDGE,"E71.filletArc"),sQuery(id+"F27.wireOp",EDGE,"E72.filletArc"),sQuery(id+"F27.wireOp",EDGE,"E73"),sQuery(id+"F27.wireOp",EDGE,"E74"),sQuery(id+"F27.wireOp",EDGE,"E75"),sQuery(id+"F27.wireOp",EDGE,"E76.filletArc"),sQuery(id+"F27.wireOp",EDGE,"E77"),sQuery(id+"F27.wireOp",EDGE,"E78.filletArc"),sQuery(id+"F27.wireOp",EDGE,"E79.MirrorCS"),sQuery(id+"F27.wireOp",EDGE,"E80.MirrorCS"),sQuery(id+"F27.wireOp",EDGE,"E81.MirrorCS"),sQuery(id+"F27.wireOp",EDGE,"E82.MirrorCS"),sQuery(id+"F27.wireOp",EDGE,"E83.MirrorCS"),sQuery(id+"F27.wireOp",EDGE,"E84.MirrorCS"),sQuery(id+"F27.wireOp",EDGE,"E85.MirrorCS"),sQuery(id+"F27.wireOp",EDGE,"E86.MirrorCS"),sQuery(id+"F27.wireOp",EDGE,"E87.MirrorCS")])]});
            hole(context, id + "F31", {"style" : HoleStyle.SIMPLE, "endStyle" : HoleEndStyle.THROUGH, "standardTappedOrClearance" : lookupTablePath({ "standard" : "ISO", "size" : "12", "type" : "Drilled" }), "standardBlindInLast" : lookupTablePath({ "standard" : "ISO", "size" : "12", "type" : "Drilled" }), "holeDiameter" : 12 * mm, "majorDiameter" : 5 * mm, "isTappedThrough" : true, "tappedDepth" : 12 * mm, "tapClearance" : 3, "startFromSketch" : true, "locations" : qUnion([Q0]), "scope" : qUnion([Q1, Q2])});
        }
        {
            var Q0;
            Q0=makeQuery(id+"F28.opExtrude","SWEPT_FACE",FACE,{"disambiguationData":[OSD([sQuery(id+"F27.wireOp",EDGE,"E74")])]});
            var sketch = newSketch(context, id + "F32", { "sketchPlane" : qUnion([Q0])});
            skLineSegment(sketch, "E95.0.0", {"start": v(720, -56.5) * mm, "end": v(720, -33.5) * mm});
            skLineSegment(sketch, "E95.0.1", {"start": v(720, -33.5) * mm, "end": v(490, -33.5) * mm});
            skLineSegment(sketch, "E95.0.2", {"start": v(490, -33.5) * mm, "end": v(490, -56.5) * mm});
            skLineSegment(sketch, "E95.0.3", {"start": v(490, -56.5) * mm, "end": v(720, -56.5) * mm});
            skLineSegment(sketch, "E96.0.0", {"start": v(720, -33.5) * mm, "end": v(720, -27.5) * mm});
            skLineSegment(sketch, "E96.0.1", {"start": v(720, -27.5) * mm, "end": v(490, -27.5) * mm});
            skLineSegment(sketch, "E96.0.2", {"start": v(490, -27.5) * mm, "end": v(490, -33.5) * mm});
            skLineSegment(sketch, "E96.0.3", {"start": v(490, -33.5) * mm, "end": v(720, -33.5) * mm});
            skLineSegment(sketch, "E97.0.0", {"start": v(720, 27.5) * mm, "end": v(720, 33.5) * mm});
            skLineSegment(sketch, "E97.0.1", {"start": v(720, 33.5) * mm, "end": v(490, 33.5) * mm});
            skLineSegment(sketch, "E97.0.2", {"start": v(490, 33.5) * mm, "end": v(490, 27.5) * mm});
            skLineSegment(sketch, "E97.0.3", {"start": v(490, 27.5) * mm, "end": v(720, 27.5) * mm});
            skLineSegment(sketch, "E98.0.0", {"start": v(720, 33.5) * mm, "end": v(720, 56.5) * mm});
            skLineSegment(sketch, "E98.0.1", {"start": v(584, 56.5) * mm, "end": v(496, 56.5) * mm});
            skLineSegment(sketch, "E98.0.2", {"start": v(490, 50.5) * mm, "end": v(490, 33.5) * mm});
            skLineSegment(sketch, "E98.0.3", {"start": v(490, 33.5) * mm, "end": v(720, 33.5) * mm});
            skPoint(sketch, "E99.0", {"position": v(720, 0) * mm});
            skPoint(sketch, "E100.0", {"position": v(490, 0) * mm});
            skLineSegment(sketch, "E101", {"start": v(490, 0) * mm, "end": v(720, 0) * mm, "construction": true});
            skLineSegment(sketch, "E102", {"start": v(590, 33.5) * mm, "end": v(590, 50.5) * mm});
            skArc(sketch, "E103.filletArc", {"start": v(590, 50.5) * mm, "mid": v(588.24, 54.74) * mm, "end": v(584, 56.5) * mm});
            skPoint(sketch, "E104.visualSharp", {"position": v(490, 56.5) * mm});
            skArc(sketch, "E104.filletArc", {"start": v(496, 56.5) * mm, "mid": v(491.76, 54.74) * mm, "end": v(490, 50.5) * mm});
            skLineSegment(sketch, "E105", {"start": v(540, 56.5) * mm, "end": v(540, 33.5) * mm, "construction": true});
            skPoint(sketch, "E105.endSnap0", {"position": v(540, 56.5) * mm});
            skLineSegment(sketch, "E106", {"start": v(505, 45) * mm, "end": v(540, 45) * mm, "construction": true});
            skPoint(sketch, "E106.startSnap0", {"position": v(540, 45) * mm});
            skLineSegment(sketch, "E107", {"start": v(540, 45) * mm, "end": v(575, 45) * mm, "construction": true});
            skLineSegment(sketch, "E108.bottom", {"start": v(505, 41.5) * mm, "end": v(575, 41.5) * mm});
            skLineSegment(sketch, "E108.top", {"start": v(505, 48.5) * mm, "end": v(575, 48.5) * mm});
            skLineSegment(sketch, "E108.left", {"start": v(505, 48.5) * mm, "end": v(505, 41.5) * mm});
            skLineSegment(sketch, "E108.right", {"start": v(575, 48.5) * mm, "end": v(575, 41.5) * mm});
            skLineSegment(sketch, "E109", {"start": v(571.5, 48.5) * mm, "end": v(571.5, 41.5) * mm, "construction": true});
            skArc(sketch, "E110", {"start": v(571.5, 41.5) * mm, "mid": v(575, 45) * mm, "end": v(571.5, 48.5) * mm});
            skArc(sketch, "E111.MirrorCS", {"start": v(508.5, 41.5) * mm, "mid": v(505, 45) * mm, "end": v(508.5, 48.5) * mm});
            skLineSegment(sketch, "E112", {"start": v(496, 56.5) * mm, "end": v(490, 56.5) * mm});
            skLineSegment(sketch, "E113", {"start": v(490, 50.5) * mm, "end": v(490, 56.5) * mm});
            skLineSegment(sketch, "E114.MirrorCS", {"start": v(590, -33.5) * mm, "end": v(590, -50.5) * mm});
            skArc(sketch, "E115.MirrorCS", {"start": v(590, -50.5) * mm, "mid": v(588.24, -54.74) * mm, "end": v(584, -56.5) * mm});
            skLineSegment(sketch, "E116.MirrorCS", {"start": v(584, -56.5) * mm, "end": v(496, -56.5) * mm});
            skArc(sketch, "E117.MirrorCS", {"start": v(496, -56.5) * mm, "mid": v(491.76, -54.74) * mm, "end": v(490, -50.5) * mm});
            skLineSegment(sketch, "E118.MirrorCS", {"start": v(490, -50.5) * mm, "end": v(490, -33.5) * mm});
            skLineSegment(sketch, "E119.MirrorCS", {"start": v(490, -50.5) * mm, "end": v(490, -56.5) * mm});
            skLineSegment(sketch, "E120.MirrorCS", {"start": v(496, -56.5) * mm, "end": v(490, -56.5) * mm});
            skArc(sketch, "E121.MirrorCS", {"start": v(508.5, -41.5) * mm, "mid": v(505, -45) * mm, "end": v(508.5, -48.5) * mm});
            skLineSegment(sketch, "E122.MirrorCS", {"start": v(505, -48.5) * mm, "end": v(575, -48.5) * mm});
            skLineSegment(sketch, "E123.MirrorCS", {"start": v(505, -41.5) * mm, "end": v(575, -41.5) * mm});
            skArc(sketch, "E124.MirrorCS", {"start": v(571.5, -41.5) * mm, "mid": v(575, -45) * mm, "end": v(571.5, -48.5) * mm});
            skLineSegment(sketch, "E125.0.1", {"start": v(720, 56.5) * mm, "end": v(490, 56.5) * mm});
            skLineSegment(sketch, "E125.0.2", {"start": v(490, 56.5) * mm, "end": v(490, 33.5) * mm});
            skLineSegment(sketch, "E126.0", {"start": v(530, 27.5) * mm, "end": v(720, 27.5) * mm});
            skLineSegment(sketch, "E127.0", {"start": v(490, -27.5) * mm, "end": v(720, -27.5) * mm});
            skLineSegment(sketch, "E128", {"start": v(590, 33.5) * mm, "end": v(590, 27.5) * mm});
            skLineSegment(sketch, "E129", {"start": v(590, -33.5) * mm, "end": v(590, -27.5) * mm});
            skLineSegment(sketch, "E130", {"start": v(590, -27.5) * mm, "end": v(720, -27.5) * mm});
            skSolve(sketch);
        }
        {
            var Q0;
            {var subQ0=sQuery(id+"F32.wireOp",EDGE,"E121.MirrorCS");Q0=makeQuery(id+"F32.imprint","IMPRINT",FACE,{"disambiguationData":[TD([[makeQuery(id+"F32.imprint","IMPRINT",EDGE,{"derivedFrom":subQ0}),1.0]])]});}
            var Q1;
            {var subQ1=sQuery(id+"F32.wireOp",EDGE,"E95.0.0");Q1=makeQuery(id+"F32.imprint","IMPRINT",FACE,{"disambiguationData":[TD([[makeQuery(id+"F32.imprint","IMPRINT",EDGE,{"derivedFrom":subQ1}),1.0]])]});}
            var Q2;
            Q2=makeQuery(id+"F32.imprint","IMPRINT",FACE,{"disambiguationData":[TD([[makeQuery(id+"F32.imprint","IMPRINT",EDGE,{"derivedFrom":sQuery(id+"F32.wireOp",EDGE,"E117.MirrorCS")}),1.0]])]});
            var Q3;
            {var subQ3=sQuery(id+"F32.wireOp",EDGE,"E102");Q3=makeQuery(id+"F32.imprint","IMPRINT",FACE,{"disambiguationData":[TD([[makeQuery(id+"F32.imprint","IMPRINT",EDGE,{"derivedFrom":subQ3}),-1.0]])]});}
            var Q4;
            {var subQ0=sQuery(id+"F32.wireOp",EDGE,"E110");var subQ1=sQuery(id+"F32.wireOp",EDGE,"E108.bottom");var subQ2=makeQuery(id+"F32.imprint","INTERSECT",VERTEX,{"derivedFrom":[subQ1,subQ0]});Q4=makeQuery(id+"F32.imprint","IMPRINT",FACE,{"disambiguationData":[TD([[makeQuery(id+"F32.imprint","IMPRINT",EDGE,{"disambiguationData":[TD([[subQ2,1.0]])],"derivedFrom":subQ1}),1.0]])]});}
            var Q5;
            {var subQ0=sQuery(id+"F32.wireOp",EDGE,"E104.filletArc");Q5=makeQuery(id+"F32.imprint","IMPRINT",FACE,{"disambiguationData":[TD([[makeQuery(id+"F32.imprint","IMPRINT",EDGE,{"derivedFrom":subQ0}),-1.0]])]});}
            extrude(context, id + "F33", {"entities" : qUnion([Q0, Q1, Q2, Q3, Q4, Q5]), "operationType" : NewBodyOperationType.REMOVE, "oppositeDirection" : true, "depth" : 25 * mm, "offsetDistance" : 25 * mm});
        }
        {
            var Q0;
            {var subQ1=sQuery(id+"F27.wireOp",EDGE,"E79.MirrorCS");Q0=makeQuery(id+"F30.boolean.opBoolean","COPY",FACE,{"disambiguationData":[TD([makeQuery(id+"F28.opExtrude","SWEPT_FACE",FACE,{"disambiguationData":[OSD([subQ1])]})])],"derivedFrom":makeQuery(id+"F30.opExtrude","SWEPT_FACE",FACE,{"disambiguationData":[OSD([sQuery(id+"F29.wireOp",EDGE,"E88.0")])]})});}
            var sketch = newSketch(context, id + "F34", { "sketchPlane" : qUnion([Q0])});
            skLineSegment(sketch, "E131.0", {"start": v(590, 33.5) * mm, "end": v(590, 50.5) * mm});
            skLineSegment(sketch, "E132.0.0", {"start": v(720, 27.5) * mm, "end": v(720, 33.5) * mm});
            skLineSegment(sketch, "E132.0.1", {"start": v(720, 33.5) * mm, "end": v(590, 33.5) * mm});
            skLineSegment(sketch, "E132.0.2", {"start": v(590, 33.5) * mm, "end": v(490, 33.5) * mm});
            skLineSegment(sketch, "E132.0.3", {"start": v(490, 33.5) * mm, "end": v(490, 27.5) * mm});
            skLineSegment(sketch, "E132.0.4", {"start": v(490, 27.5) * mm, "end": v(720, 27.5) * mm});
            skLineSegment(sketch, "E133.0.0", {"start": v(720, -33.5) * mm, "end": v(720, -27.5) * mm});
            skLineSegment(sketch, "E133.0.1", {"start": v(720, -27.5) * mm, "end": v(490, -27.5) * mm});
            skLineSegment(sketch, "E133.0.2", {"start": v(490, -27.5) * mm, "end": v(490, -33.5) * mm});
            skLineSegment(sketch, "E133.0.3", {"start": v(490, -33.5) * mm, "end": v(590, -33.5) * mm});
            skLineSegment(sketch, "E133.0.4", {"start": v(590, -33.5) * mm, "end": v(720, -33.5) * mm});
            skLineSegment(sketch, "E134.0", {"start": v(590, -33.5) * mm, "end": v(590, -50.5) * mm});
            skPoint(sketch, "E135.0", {"position": v(590, -33.5) * mm});
            skPoint(sketch, "E136.0", {"position": v(590, 33.5) * mm});
            skLineSegment(sketch, "E137", {"start": v(590, 33.5) * mm, "end": v(590, -33.5) * mm});
            skSolve(sketch);
        }
        {
            var Q0;
            {var subQ0=sQuery(id+"F34.wireOp",EDGE,"E133.0.0");Q0=makeQuery(id+"F34.imprint","IMPRINT",FACE,{"disambiguationData":[TD([[makeQuery(id+"F34.imprint","IMPRINT",EDGE,{"derivedFrom":subQ0}),1.0]])]});}
            var Q1;
            {var subQ0=sQuery(id+"F34.wireOp",EDGE,"E132.0.0");Q1=makeQuery(id+"F34.imprint","IMPRINT",FACE,{"disambiguationData":[TD([[makeQuery(id+"F34.imprint","IMPRINT",EDGE,{"derivedFrom":subQ0}),1.0]])]});}
            extrude(context, id + "F35", {"entities" : qUnion([Q0, Q1]), "operationType" : NewBodyOperationType.REMOVE, "oppositeDirection" : true, "depth" : 100 * mm, "offsetDistance" : 25 * mm});
        }
    });
